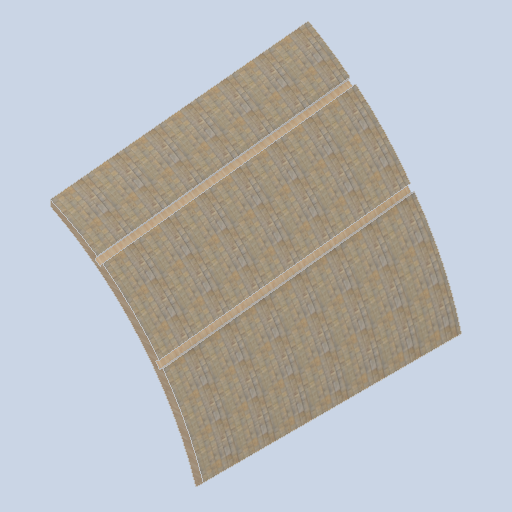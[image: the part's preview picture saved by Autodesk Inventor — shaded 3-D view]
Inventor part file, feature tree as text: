
AUTODESK INVENTOR PART (.ipt)
format: ipt  version: 2024.2 (Build 282272000, 272)  size: 363,520 bytes
history: native  units: in
note: dims shown in document units (in); Inventor stores cm internally (conversion verified against a paired STEP export)
features: other x3, sketch x2, plane x2
ambient origin geometry x8: Origin, YZ Plane, XZ Plane, XY Plane, X Axis, Y Axis, Z Axis, Center Point
bodies: Solid1 (feature_tree)
feature tree (7):
  other  "panel_block_02_MIR.ipt"
  other  "Solid1::panel_block_02_MIR.ipt"
  other  "TaggingFeature1"
  sketch  "Sketch1"  dims[d0=0.3937in]
  sketch  "Sketch2"
  plane  "Work Plane1"
  plane  "Work Plane2"
